# Revit family: STL21701BR_30_40_50
name_source: partatom
category: Luminárias
units: mm (PartAtom-declared; Revit-internal decimal feet)

## family parameters
Compartilhado = Não
Corte com vazios quando carregada = Não
Cota do conector redondo = Utilizar diâmetro
Fonte luminosa = Não
Hospedeiro = Parede
Manter orientação da anotação = Não
Número OmniClass = 23.80.70.00
Ponto de cálculo do ambiente = Não
Sempre na vertical = Sim
Tipo de parte = Normal
Título OmniClass = Lighting

## types (3) — shared parameters
Altura = 0.2 m
Comprimento = 0.08 m
Dimerização = Não dimerizável
Estrutura = Al - Branco
Fabricante = Stella
Grau de proteção (IP) = IP65
IRC (Índice de reprodução de cores) = >80
Largura = 0.04 m
Modelo = ICE
Potência = 5 W
Tensão Elétrica = 100V-240V
URL = https://stella.com.br
Ângulo de Abertura = 120°
zero-valued in all types: Elevação padrão

## per-type parameters (varying)
| type | Fluxo Luminoso | Luminoso | Referência | Temperatura da cor (K) |
| STL21701BR/30 - BRANCO - BIVOLT - 3000K - 540lm | 540 lm | Emissivo 3000K (ICE) | STL21701BR/30 - BIVOLT | 3000 K |
| STL21701BR/40 - BRANCO - BIVOLT - 4000K - 560lm | 560 lm | Emissivo 4000K (ICE) | STL21701BR/40 - BIVOLT | 4000 K |
| STL21701BR/50 - BRANCO - BIVOLT - 5000K - 580lm | 580 lm | Emissivo 5000K (ICE) | STL21701BR/50 - BIVOLT | 5000 K |
